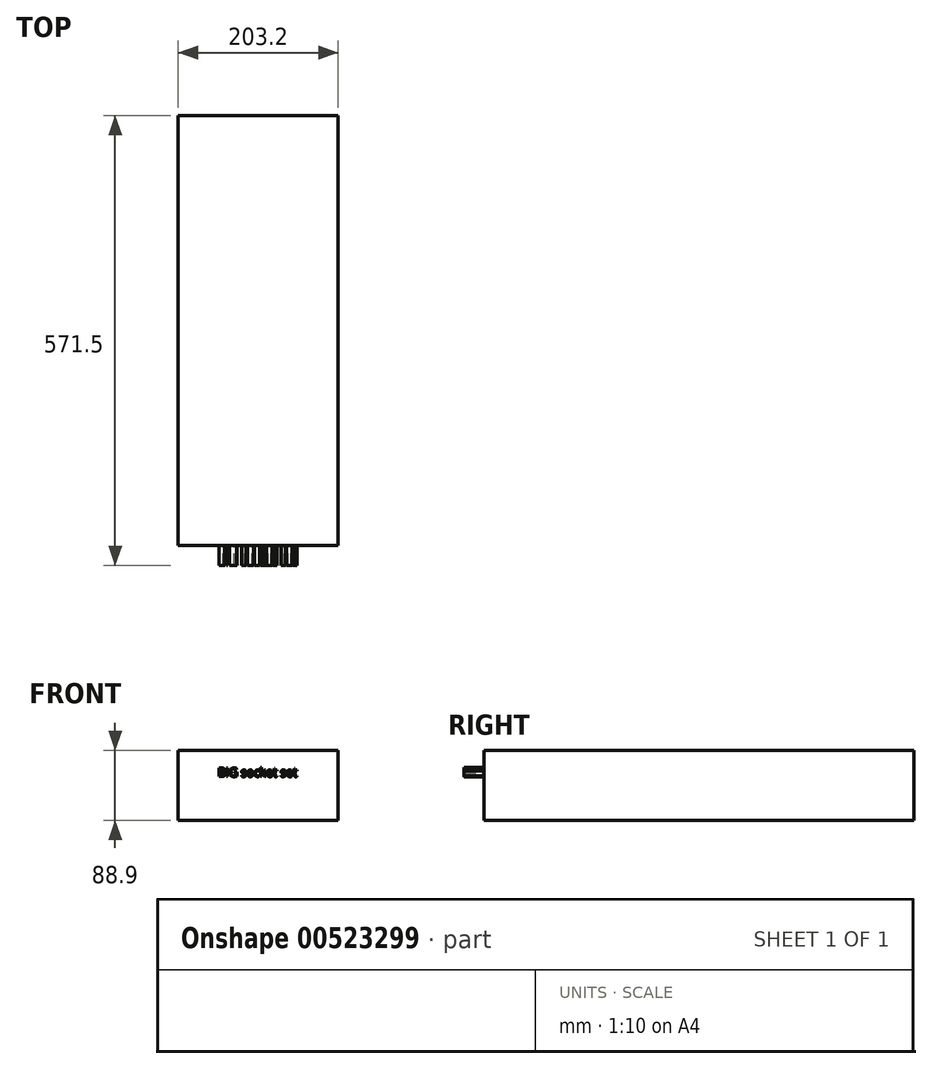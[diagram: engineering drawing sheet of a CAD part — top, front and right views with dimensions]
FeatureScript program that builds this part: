
annotation { "Feature Type Name" : "Feature", "Feature Type Description" : "" }
export const myFeature = defineFeature(function(context is Context, id is Id, definition is map)
    precondition{}
    {
        {
            var Q0;
            Q0=qCreatedBy(makeId("Front.planeOp"),FACE);
            var sketch = newSketch(context, id + "F0", { "sketchPlane" : qUnion([Q0])});
            skLineSegment(sketch, "E0.bottom", {"start": v(101.6, 44.45) * mm, "end": v(-101.6, 44.45) * mm});
            skLineSegment(sketch, "E0.top", {"start": v(101.6, -44.45) * mm, "end": v(-101.6, -44.45) * mm});
            skLineSegment(sketch, "E0.left", {"start": v(101.6, 44.45) * mm, "end": v(101.6, -44.45) * mm});
            skLineSegment(sketch, "E0.right", {"start": v(-101.6, 44.45) * mm, "end": v(-101.6, -44.45) * mm});
            skPoint(sketch, "E0.middle", {"position": v(0, 0) * mm});
            skSolve(sketch);
        }
        {
            var Q0;
            Q0=makeQuery(id+"F0.imprint","IMPRINT",FACE,{"disambiguationData":[TD([[makeQuery(id+"F0.imprint","IMPRINT",EDGE,{"derivedFrom":sQuery(id+"F0.wireOp",EDGE,"E0.bottom")}),1.0]])]});
            extrude(context, id + "F1", {"entities" : qUnion([Q0]), "depth" : 546.1 * mm, "offsetDistance" : 25.4 * mm});
        }
        {
            var Q0;
            Q0=makeQuery(id+"F1.opExtrude","CAP_FACE",FACE,{"disambiguationData":[OSD([sQuery(id+"F0.wireOp",EDGE,"E0.bottom"),sQuery(id+"F0.wireOp",EDGE,"E0.top"),sQuery(id+"F0.wireOp",EDGE,"E0.left"),sQuery(id+"F0.wireOp",EDGE,"E0.right")])],"isStart":false});
            var sketch = newSketch(context, id + "F2", { "sketchPlane" : qUnion([Q0])});
            skText(sketch, "E1", { "text": "BIG socket set", "fontName": "OpenSans-Regular.ttf"});
            const initialGuessF2  = {"E1": [-0.05139, 0.01114, 1, 0, 0.01107]};
            skSetInitialGuess(sketch, initialGuessF2);
            skSolve(sketch);
        }
        {
            var Q0;
            Q0 = qSketchRegion(id + "F2", true);
            extrude(context, id + "F3", {"entities" : qUnion([Q0]), "operationType" : NewBodyOperationType.ADD, "depth" : 25.4 * mm, "offsetDistance" : 25.4 * mm});
        }
    });
